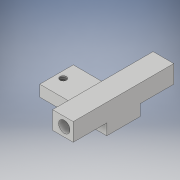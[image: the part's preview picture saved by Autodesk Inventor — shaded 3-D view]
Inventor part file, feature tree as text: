
AUTODESK INVENTOR PART (.ipt)
format: ipt  version: 2019 (Build 230136000, 136)  size: 135,168 bytes
history: native  units: in
note: dims shown in document units (in); Inventor stores cm internally (conversion verified against a paired STEP export)
features: sketch x4, extrude x2, hole x2, projected_geometry x2, fillet x1
ambient origin geometry x8: Origin, YZ Plane, XZ Plane, XY Plane, X Axis, Y Axis, Z Axis, Center Point
bodies: Solid1 (feature_tree)
feature tree (11):
  extrude  "Extrusion1"  Depth=0.75in
  extrude  "Extrusion2"  Depth=0.4in TaperAngle=0.0deg
  hole  "Hole1"  [1 undecoded]
  hole  "Hole2"  [1 undecoded]
  fillet  "Fillet2"  Radius=1.5in
  sketch  "Sketch1"  dims[d0=1.5in d1=0.75in]
  sketch  "Sketch2"  dims[d2=0.25in d3=0.0in d5=0.4in d6=0.0in]
  sketch  "Sketch3"  dims[d7=0.4in d9=0.2in]
  projected_geometry  "Projected Loop1"
  sketch  "Sketch4"  dims[d11=0.255in d12=0.75in d13=0.375in d14=0.25in d15=0.5635in d16=1.0in d17=0.8108in d22=0.75in d23=0.75in d24=1.5in d25=0.375in d26=0.375in d27=0.15in d28=0.145in d29=0.38in d30=0.375in d31=0.25in d32=0.5635in d33=0.588in d34=0.8108in d35=0.15in d37=0.125in d38=0.75in]
  projected_geometry  "Projected Loop2"
note: 2 required parameter values undecoded (feature->parameter linkage not recoverable at this tier; creation-order binding heuristic only, values carry confidence <= 0.55)
